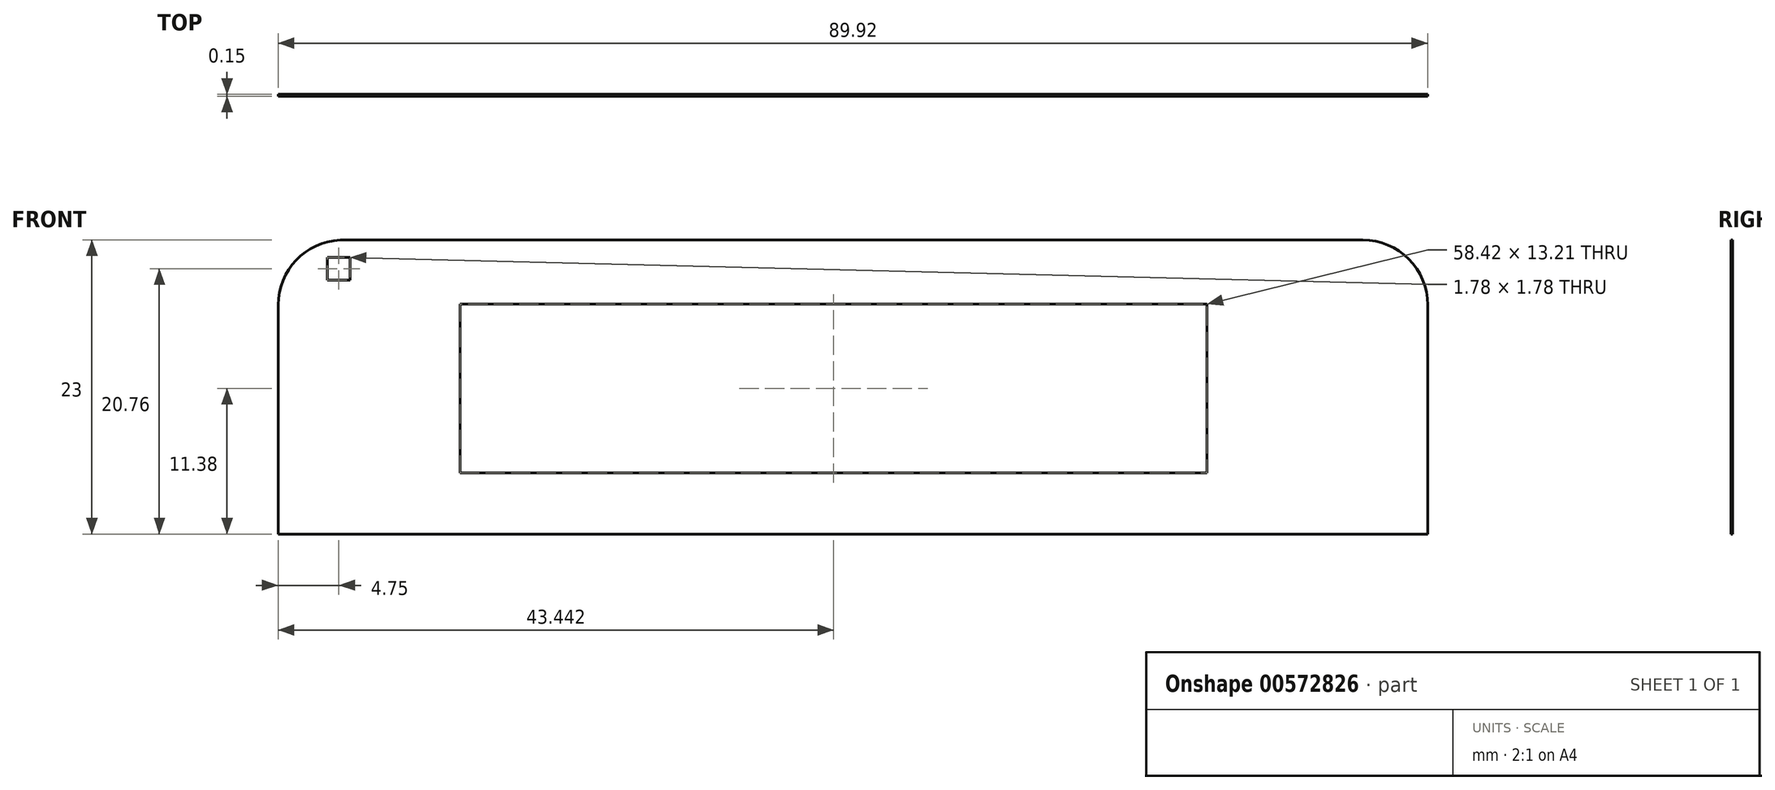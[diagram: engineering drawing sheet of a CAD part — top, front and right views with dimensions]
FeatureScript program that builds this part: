
annotation { "Feature Type Name" : "Feature", "Feature Type Description" : "" }
export const myFeature = defineFeature(function(context is Context, id is Id, definition is map)
    precondition{}
    {
        {
            var Q0;
            Q0=qCreatedBy(makeId("Front.planeOp"),FACE);
            var sketch = newSketch(context, id + "F0", { "sketchPlane" : qUnion([Q0])});
            skLineSegment(sketch, "E0.bottom", {"start": v(-27.5, 5.03) * mm, "end": v(52.5, 5.03) * mm});
            skLineSegment(sketch, "E1.bottom", {"start": v(-18.12, 0.01) * mm, "end": v(40.3, 0.01) * mm});
            skLineSegment(sketch, "E1.top", {"start": v(-18.12, -13.2) * mm, "end": v(40.3, -13.2) * mm});
            skLineSegment(sketch, "E1.left", {"start": v(-18.12, 0.01) * mm, "end": v(-18.12, -13.2) * mm});
            skLineSegment(sketch, "E1.right", {"start": v(40.3, 0.01) * mm, "end": v(40.3, -13.2) * mm});
            skLineSegment(sketch, "E2", {"start": v(-32.35, -17.97) * mm, "end": v(-32.35, -0.05) * mm});
            skLineSegment(sketch, "E3", {"start": v(-32.35, -17.97) * mm, "end": v(57.57, -17.97) * mm});
            skLineSegment(sketch, "E4", {"start": v(57.57, -17.97) * mm, "end": v(57.57, -0.05) * mm});
            skPoint(sketch, "E5.visualSharp", {"position": v(57.57, 5.03) * mm});
            skArc(sketch, "E5.filletArc", {"start": v(57.57, -0.05) * mm, "mid": v(56.08, 3.54) * mm, "end": v(52.5, 5.03) * mm});
            skArc(sketch, "E6", {"start": v(-32.35, -0.05) * mm, "mid": v(-30.94, 3.46) * mm, "end": v(-27.5, 5.03) * mm});
            skLineSegment(sketch, "E7.bottom", {"start": v(-28.49, 3.68) * mm, "end": v(-26.71, 3.68) * mm});
            skLineSegment(sketch, "E7.top", {"start": v(-28.49, 1.9) * mm, "end": v(-26.71, 1.9) * mm});
            skLineSegment(sketch, "E7.left", {"start": v(-28.49, 3.68) * mm, "end": v(-28.49, 1.9) * mm});
            skLineSegment(sketch, "E7.right", {"start": v(-26.71, 3.68) * mm, "end": v(-26.71, 1.9) * mm});
            skSolve(sketch);
        }
        {
            var Q0;
            Q0=makeQuery(id+"F0.imprint","IMPRINT",FACE,{"disambiguationData":[TD([[makeQuery(id+"F0.imprint","IMPRINT",EDGE,{"derivedFrom":sQuery(id+"F0.wireOp",EDGE,"E0.bottom")}),-1.0]])]});
            extrude(context, id + "F1", {"entities" : qUnion([Q0]), "depth" : 0.15 * mm, "offsetDistance" : 25.4 * mm});
        }
    });
